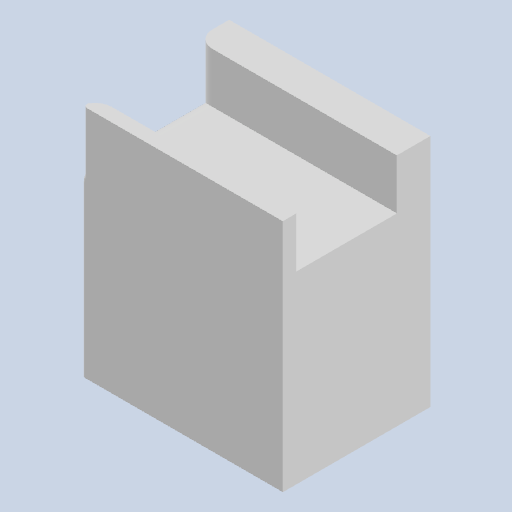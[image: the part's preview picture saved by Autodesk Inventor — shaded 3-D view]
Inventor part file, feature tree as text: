
AUTODESK INVENTOR PART (.ipt)
format: ipt  version: 2022 (Build 260153000, 153)  size: 153,600 bytes
history: native  units: mm
features: other x5, extrude x4, sketch x4, reference x3, fillet x2, projected_geometry x2
ambient origin geometry x8: Origin, YZ Plane, XZ Plane, XY Plane, X Axis, Y Axis, Z Axis, Center Point
bodies: Body1 (feature_tree)
feature tree (20):
  other  "Твердое тело1"
  extrude  "Выдавливание1"  Depth=12.0mm
  extrude  "Выдавливание2"  Depth=10.0mm TaperAngle=0.0deg
  extrude  "Выдавливание3"  Depth=4.2mm
  fillet  "Сопряжение1"  Radius=11.0mm
  extrude  "Выдавливание4"  Depth=2.0mm
  fillet  "Сопряжение2"  Radius=2.0mm
  sketch  "Эскиз1"
  reference  "Ссылка1"
  reference  "Ссылка2"
  sketch  "Эскиз2"
  projected_geometry  "Спроецированная петля1"
  sketch  "Эскиз3"
  projected_geometry  "Спроецированная петля2"
  sketch  "Эскиз4"
  reference  "Ссылка3"
  other  "<userpath>\Documents\Git\MZCAT_2024\MZCAT_4.iam"
  other  "MZCAT_4.iam"
  other  "upor:1"
  other  "base:1"
